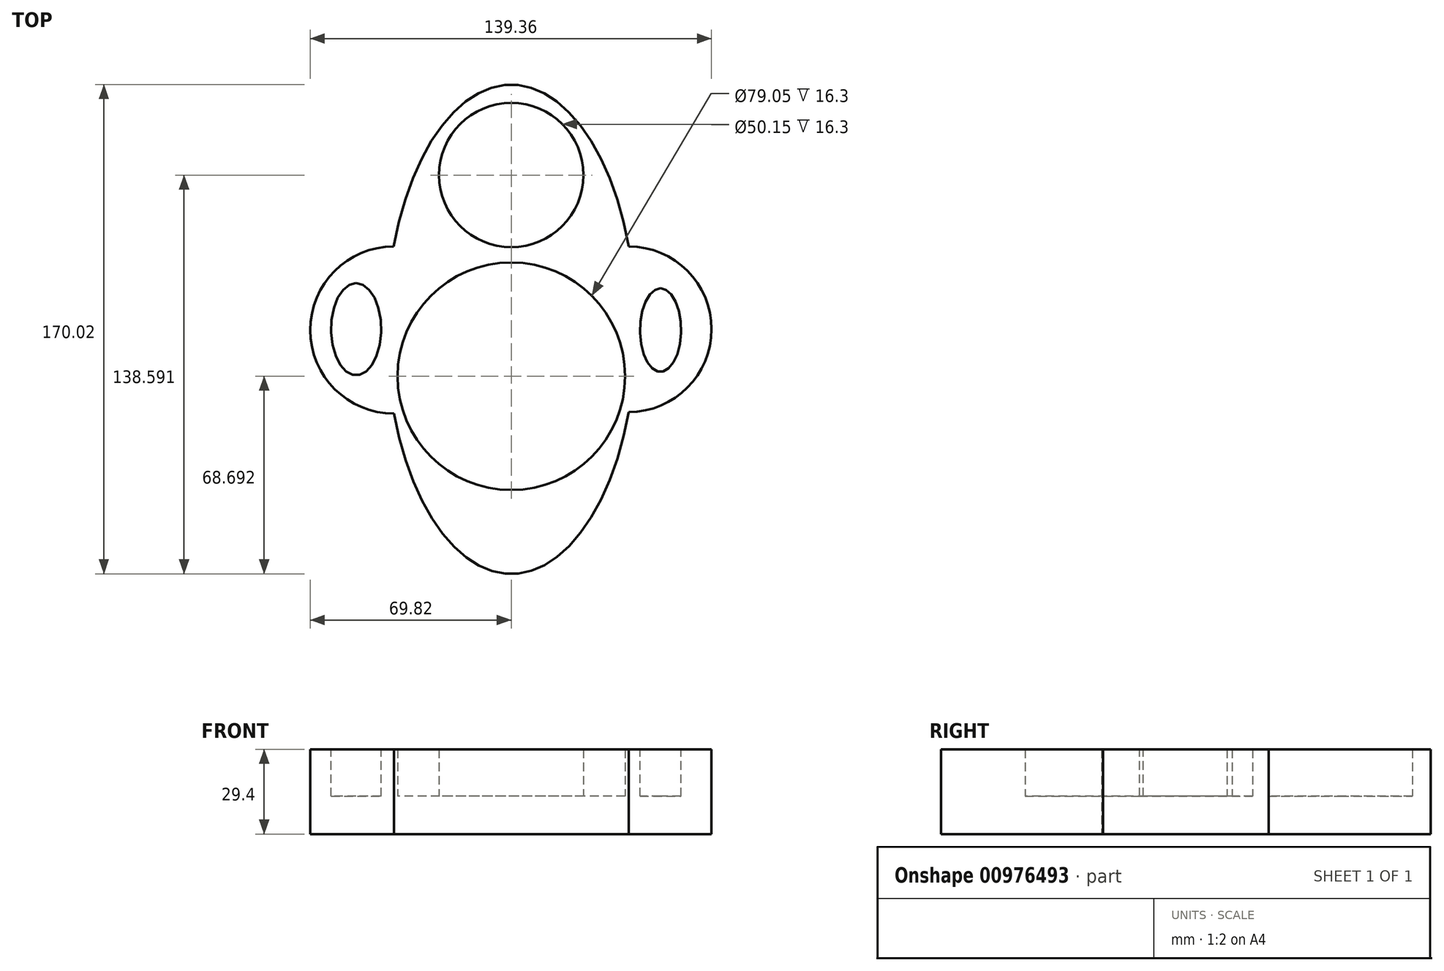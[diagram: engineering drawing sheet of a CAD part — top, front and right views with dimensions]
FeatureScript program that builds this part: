
annotation { "Feature Type Name" : "Feature", "Feature Type Description" : "" }
export const myFeature = defineFeature(function(context is Context, id is Id, definition is map)
    precondition{}
    {
        {
            var Q0;
            Q0=qCreatedBy(makeId("Top.planeOp"),FACE);
            var sketch = newSketch(context, id + "F0", { "sketchPlane" : qUnion([Q0])});
            skPoint(sketch, "E0.middle", {"position": v(0, 0) * mm});
            skEllipse(sketch, "E1", {"center": v(0, 0) * mm, "majorRadius": 85.01 * mm, "minorRadius": 43.4 * mm, "majorAxis": v(0, -1)});
            skArc(sketch, "E2", {"start": v(-40.79, 28.75) * mm, "mid": v(-69.82, -0.3) * mm, "end": v(-40.74, -29.3) * mm});
            skArc(sketch, "E3", {"start": v(40.79, 28.75) * mm, "mid": v(69.54, 0) * mm, "end": v(40.79, -28.75) * mm});
            skPoint(sketch, "E0.top.start.orphan", {"position": v(-40.79, -28.75) * mm});
            skCircle(sketch, "E4", {"center": v(0, 53.58) * mm, "radius": 25.07 * mm});
            skCircle(sketch, "E5", {"center": v(0, -16.32) * mm, "radius": 39.52 * mm});
            skEllipse(sketch, "E6", {"center": v(-53.89, 0) * mm, "majorRadius": 16.03 * mm, "minorRadius": 8.7 * mm, "majorAxis": v(0, 1)});
            skEllipse(sketch, "E7", {"center": v(51.82, -0.28) * mm, "majorRadius": 14.52 * mm, "minorRadius": 7.12 * mm, "majorAxis": v(0, 1)});
            skSolve(sketch);
        }
        {
            var Q0;
            Q0 = qSketchRegion(id + "F0", true);
            extrude(context, id + "F1", {"entities" : qUnion([Q0]), "depth" : 29.4 * mm, "offsetDistance" : 25 * mm});
        }
        {
            var Q0;
            Q0 = qSketchRegion(id + "F0", true);
            var Q1;
            Q1=makeQuery(id+"F0.imprint","IMPRINT",FACE,{"disambiguationData":[TD([[makeQuery(id+"F0.imprint","IMPRINT",EDGE,{"derivedFrom":sQuery(id+"F0.wireOp",EDGE,"E7")}),1.0]])]});
            var Q2;
            Q2=makeQuery(id+"F0.imprint","IMPRINT",FACE,{"disambiguationData":[TD([[makeQuery(id+"F0.imprint","IMPRINT",EDGE,{"derivedFrom":sQuery(id+"F0.wireOp",EDGE,"E5")}),1.0]])]});
            var Q3;
            Q3=makeQuery(id+"F0.imprint","IMPRINT",FACE,{"disambiguationData":[TD([[makeQuery(id+"F0.imprint","IMPRINT",EDGE,{"derivedFrom":sQuery(id+"F0.wireOp",EDGE,"E4")}),1.0]])]});
            var Q4;
            Q4=makeQuery(id+"F0.imprint","IMPRINT",FACE,{"disambiguationData":[TD([[makeQuery(id+"F0.imprint","IMPRINT",EDGE,{"derivedFrom":sQuery(id+"F0.wireOp",EDGE,"E6")}),1.0]])]});
            extrude(context, id + "F2", {"entities" : qUnion([Q0, Q1, Q2, Q3, Q4]), "operationType" : NewBodyOperationType.ADD, "depth" : 13.1 * mm, "offsetDistance" : 25 * mm});
        }
    });
